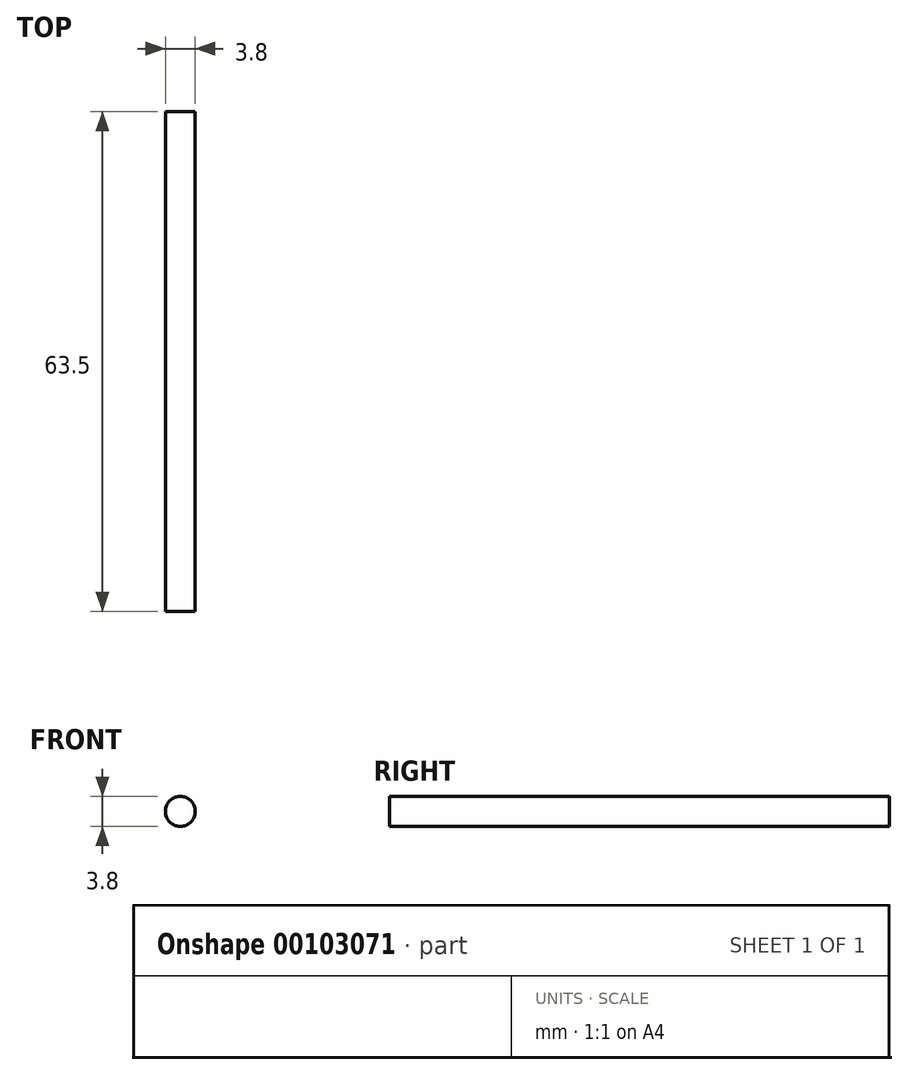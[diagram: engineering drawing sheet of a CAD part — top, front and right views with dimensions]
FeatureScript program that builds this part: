
annotation { "Feature Type Name" : "Feature", "Feature Type Description" : "" }
export const myFeature = defineFeature(function(context is Context, id is Id, definition is map)
    precondition{}
    {
        {
            var Q0;
            Q0=qCreatedBy(makeId("Top.planeOp"),FACE);
            var sketch = newSketch(context, id + "F0", { "sketchPlane" : qUnion([Q0])});
            skLineSegment(sketch, "E0", {"start": v(-11.51, 72.58) * mm, "end": v(-11.51, 9.08) * mm});
            skLineSegment(sketch, "E1", {"start": v(-9.61, 72.58) * mm, "end": v(-9.61, 37.16) * mm});
            skLineSegment(sketch, "E2", {"start": v(-9.61, 37.16) * mm, "end": v(-9.61, 9.08) * mm});
            skLineSegment(sketch, "E3", {"start": v(-11.51, 72.58) * mm, "end": v(-9.61, 72.58) * mm});
            skLineSegment(sketch, "E4", {"start": v(-11.51, 37.16) * mm, "end": v(-9.61, 37.16) * mm});
            skLineSegment(sketch, "E5", {"start": v(-11.51, 9.08) * mm, "end": v(-9.61, 9.08) * mm});
            skSolve(sketch);
        }
        {
            var Q0;
            Q0 = qSketchRegion(id + "F0", true);
            var Q1;
            Q1 = qConstructionFilter(qBodyType(qCreatedBy(id + "F0" ,EDGE), BodyType.WIRE), ConstructionObject.NO);
            var Q2;
            Q2=sQuery(id+"F0.wireOp",EDGE,"E0");
            revolve(context, id + "F1", {"entities" : qUnion([Q0]), "surfaceEntities" : qUnion([Q1]), "axis" : qUnion([Q2]), "revolveType" : RevolveType.FULL});
        }
    });
